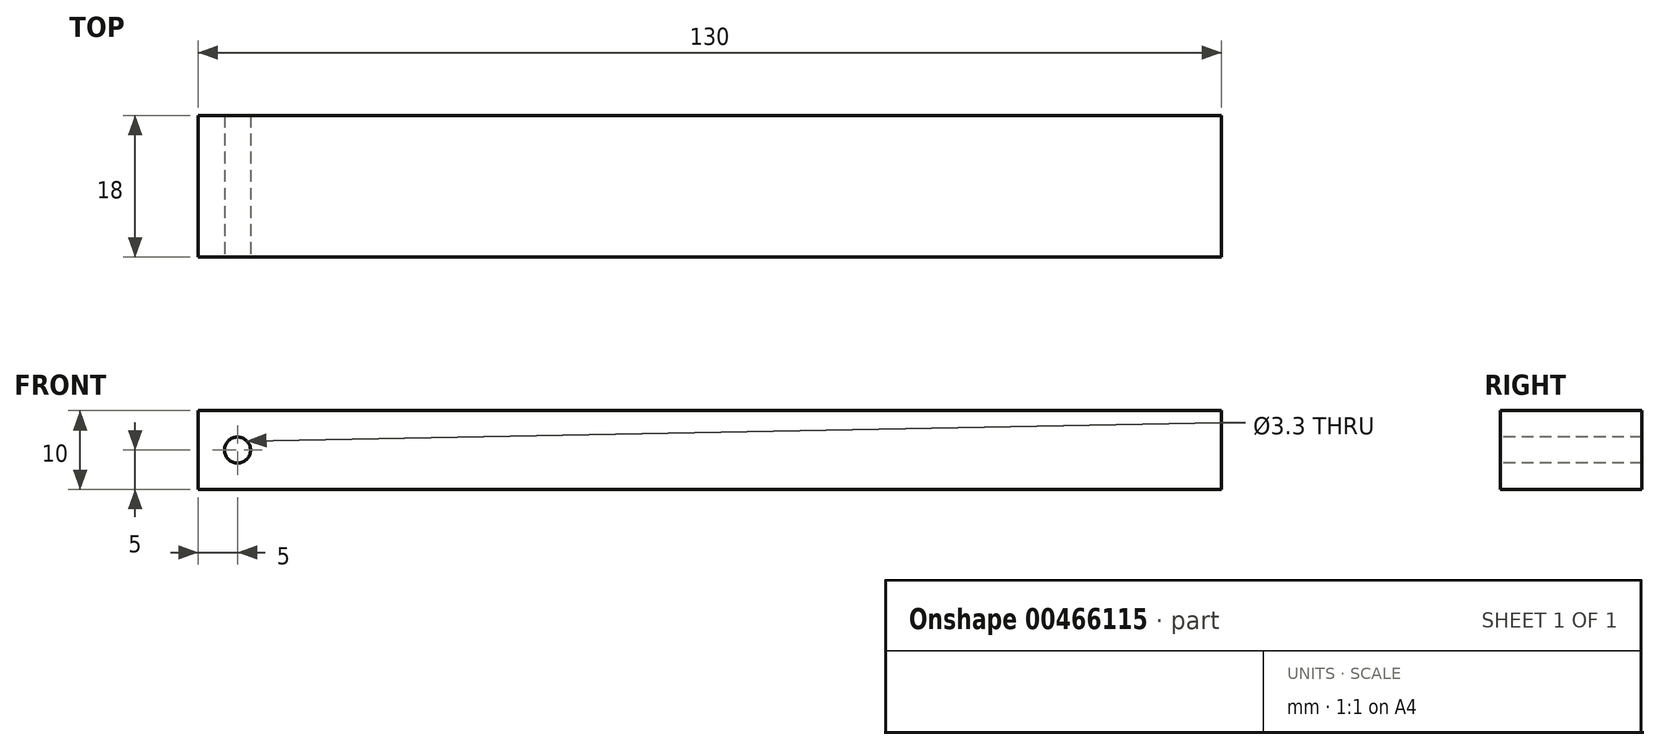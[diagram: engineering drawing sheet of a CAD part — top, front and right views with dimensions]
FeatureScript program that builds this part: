
annotation { "Feature Type Name" : "Feature", "Feature Type Description" : "" }
export const myFeature = defineFeature(function(context is Context, id is Id, definition is map)
    precondition{}
    {
        {
            var Q0;
            Q0=qCreatedBy(makeId("Top.planeOp"),FACE);
            var sketch = newSketch(context, id + "F0", { "sketchPlane" : qUnion([Q0])});
            skLineSegment(sketch, "E0", {"start": v(0, 18) * mm, "end": v(130, 18) * mm});
            skLineSegment(sketch, "E1", {"start": v(130, 18) * mm, "end": v(130, 0) * mm});
            skLineSegment(sketch, "E2", {"start": v(130, 0) * mm, "end": v(0, 0) * mm});
            skLineSegment(sketch, "E3", {"start": v(0, 18) * mm, "end": v(0, 0) * mm});
            skSolve(sketch);
        }
        {
            var Q0;
            Q0=makeQuery(id+"F0.imprint","IMPRINT",FACE,{"disambiguationData":[TD([[makeQuery(id+"F0.imprint","IMPRINT",EDGE,{"derivedFrom":sQuery(id+"F0.wireOp",EDGE,"E0")}),-1.0]])]});
            extrude(context, id + "F1", {"entities" : qUnion([Q0]), "depth" : 10 * mm});
        }
        {
            var Q0;
            Q0=makeQuery(id+"F1.opExtrude","SWEPT_FACE",FACE,{"disambiguationData":[OSD([sQuery(id+"F0.wireOp",EDGE,"E2")])]});
            var sketch = newSketch(context, id + "F2", { "sketchPlane" : qUnion([Q0])});
            skLineSegment(sketch, "E4", {"start": v(0, 5) * mm, "end": v(5, 5) * mm, "construction": true});
            skLineSegment(sketch, "E5", {"start": v(5, 5) * mm, "end": v(5, 0) * mm, "construction": true});
            skCircle(sketch, "E6", {"center": v(5, 5) * mm, "radius": 1.5 * mm});
            skSolve(sketch);
        }
        {
            var Q0;
            Q0=sQuery(id+"F2.wireOp",VERTEX,"E6.center");
            var Q1;
            Q1=makeQuery(id+"F1.opExtrude","SWEPT_BODY",BODY,{"disambiguationData":[OSD([sQuery(id+"F0.wireOp",EDGE,"E0"),sQuery(id+"F0.wireOp",EDGE,"E1"),sQuery(id+"F0.wireOp",EDGE,"E2"),sQuery(id+"F0.wireOp",EDGE,"E3")])]});
            hole(context, id + "F3", {"style" : HoleStyle.SIMPLE, "endStyle" : HoleEndStyle.THROUGH, "standardTappedOrClearance" : lookupTablePath({ "standard" : "ISO", "fit" : "Normal", "size" : "M3", "type" : "Clearance" }), "standardBlindInLast" : lookupTablePath({ "fit" : "Standard", "standard" : "ISO", "size" : "M3", "type" : "Clearance" }), "holeDiameter" : 3.3 * mm, "isTappedThrough" : true, "tappedDepth" : 12 * mm, "tapClearance" : 3, "locations" : qUnion([Q0]), "scope" : qUnion([Q1])});
        }
    });
